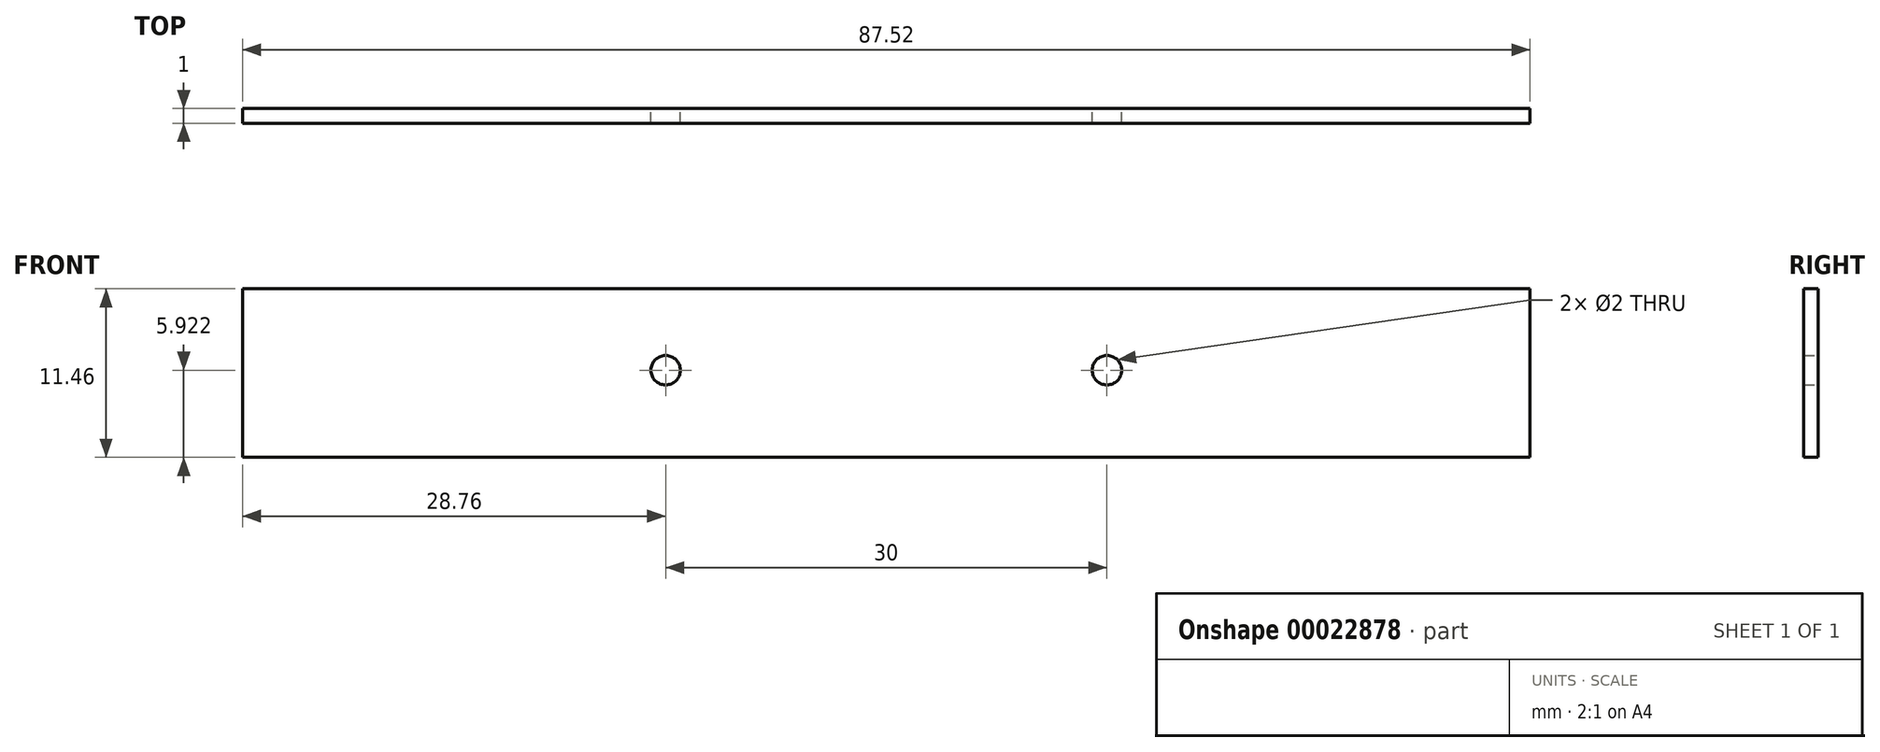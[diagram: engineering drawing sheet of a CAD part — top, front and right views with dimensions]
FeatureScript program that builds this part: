
annotation { "Feature Type Name" : "Feature", "Feature Type Description" : "" }
export const myFeature = defineFeature(function(context is Context, id is Id, definition is map)
    precondition{}
    {
        {
            var Q0;
            Q0=qCreatedBy(makeId("Front.planeOp"),FACE);
            var sketch = newSketch(context, id + "F0", { "sketchPlane" : qUnion([Q0])});
            skLineSegment(sketch, "E0.bottom", {"start": v(-43.76, 30.47) * mm, "end": v(43.76, 30.47) * mm});
            skLineSegment(sketch, "E0.top", {"start": v(-43.76, 19) * mm, "end": v(43.76, 19) * mm});
            skLineSegment(sketch, "E0.left", {"start": v(-43.76, 30.47) * mm, "end": v(-43.76, 19) * mm});
            skLineSegment(sketch, "E0.right", {"start": v(43.76, 30.47) * mm, "end": v(43.76, 19) * mm});
            skCircle(sketch, "E1", {"center": v(-15, 24.93) * mm, "radius": 1 * mm});
            skCircle(sketch, "E2", {"center": v(15, 24.93) * mm, "radius": 1 * mm});
            skSolve(sketch);
        }
        {
            var Q0;
            Q0 = qSketchRegion(id + "F0", true);
            extrude(context, id + "F1", {"entities" : qUnion([Q0]), "endBound" : BoundingType.SYMMETRIC, "depth" : 1 * mm});
        }
    });
